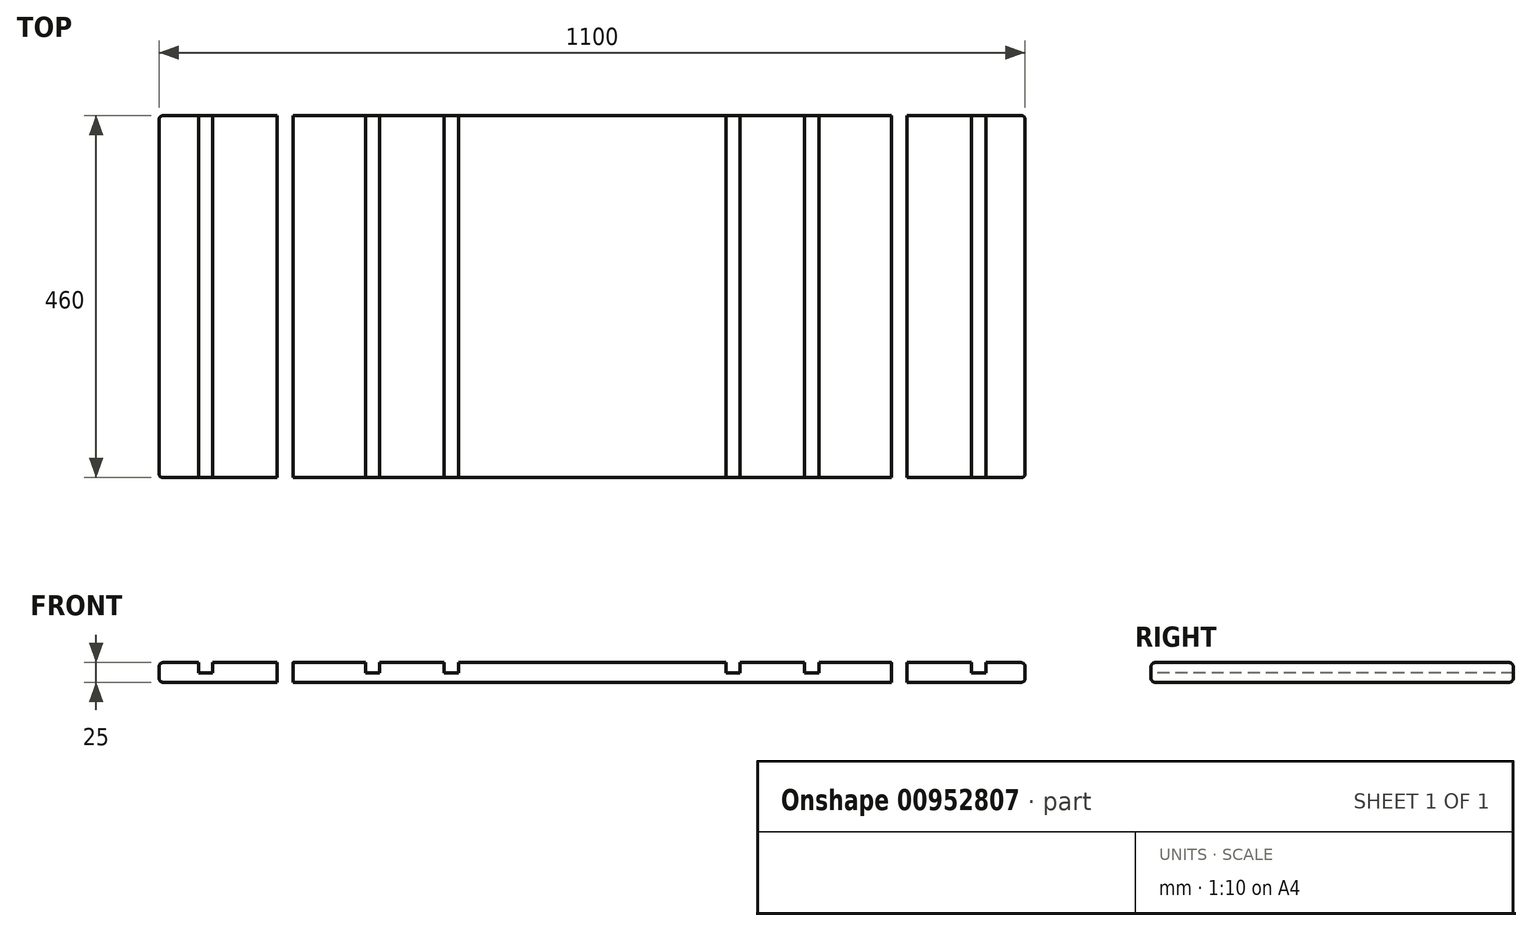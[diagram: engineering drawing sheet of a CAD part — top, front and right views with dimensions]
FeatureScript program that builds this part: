
annotation { "Feature Type Name" : "Feature", "Feature Type Description" : "" }
export const myFeature = defineFeature(function(context is Context, id is Id, definition is map)
    precondition{}
    {
        {
            var Q0;
            Q0=qCreatedBy(makeId("Top.planeOp"),FACE);
            var sketch = newSketch(context, id + "F0", { "sketchPlane" : qUnion([Q0])});
            skLineSegment(sketch, "E0.bottom", {"start": v(-380, 230) * mm, "end": v(380, 230) * mm});
            skLineSegment(sketch, "E0.top", {"start": v(-380, -230) * mm, "end": v(380, -230) * mm});
            skLineSegment(sketch, "E0.left", {"start": v(-380, 230) * mm, "end": v(-380, -230) * mm});
            skLineSegment(sketch, "E0.right", {"start": v(380, 230) * mm, "end": v(380, -230) * mm});
            skPoint(sketch, "E0.middle", {"position": v(0, 0) * mm});
            skSolve(sketch);
        }
        {
            var Q0;
            Q0=makeQuery(id+"F0.imprint","IMPRINT",FACE,{"disambiguationData":[TD([[makeQuery(id+"F0.imprint","IMPRINT",EDGE,{"derivedFrom":sQuery(id+"F0.wireOp",EDGE,"E0.bottom")}),-1.0]])]});
            extrude(context, id + "F1", {"entities" : qUnion([Q0]), "depth" : 25 * mm, "offsetDistance" : 25 * mm});
        }
        {
            var Q0;
            Q0=makeQuery(id+"F1.opExtrude","CAP_EDGE",EDGE,{"disambiguationData":[OSD([sQuery(id+"F0.wireOp",EDGE,"E0.top")])],"isStart":false});
            var Q1;
            Q1=makeQuery(id+"F1.opExtrude","CAP_EDGE",EDGE,{"disambiguationData":[OSD([sQuery(id+"F0.wireOp",EDGE,"E0.bottom")])],"isStart":false});
            var Q2;
            Q2=makeQuery(id+"F1.opExtrude","CAP_EDGE",EDGE,{"disambiguationData":[OSD([sQuery(id+"F0.wireOp",EDGE,"E0.bottom")])],"isStart":true});
            var Q3;
            Q3=makeQuery(id+"F1.opExtrude","CAP_EDGE",EDGE,{"disambiguationData":[OSD([sQuery(id+"F0.wireOp",EDGE,"E0.top")])],"isStart":true});
            fillet(context, id + "F2", {"entities" : qUnion([Q0, Q1, Q2, Q3]), "radius" : 5 * mm, "tangentPropagation" : true, "allowEdgeOverflow" : false});
        }
        {
            var Q0;
            Q0=qCreatedBy(makeId("Front.planeOp"),FACE);
            var sketch = newSketch(context, id + "F3", { "sketchPlane" : qUnion([Q0])});
            skLineSegment(sketch, "E1", {"start": v(0, 0) * mm, "end": v(-170, 0) * mm, "construction": true});
            skLineSegment(sketch, "E2", {"start": v(-170, 0) * mm, "end": v(-270, 0) * mm, "construction": true});
            skLineSegment(sketch, "E3", {"start": v(-170, 0) * mm, "end": v(-170, 25) * mm, "construction": true});
            skLineSegment(sketch, "E4", {"start": v(-270, 0) * mm, "end": v(-270, 25) * mm, "construction": true});
            skLineSegment(sketch, "E5", {"start": v(0, 0) * mm, "end": v(0, 16.31) * mm, "construction": true});
            skLineSegment(sketch, "E6.bottom", {"start": v(-170, 25) * mm, "end": v(-188, 25) * mm});
            skLineSegment(sketch, "E6.top", {"start": v(-170, 12) * mm, "end": v(-188, 12) * mm});
            skLineSegment(sketch, "E6.left", {"start": v(-170, 25) * mm, "end": v(-170, 12) * mm});
            skLineSegment(sketch, "E6.right", {"start": v(-188, 25) * mm, "end": v(-188, 12) * mm});
            skLineSegment(sketch, "E7.bottom", {"start": v(-270, 25) * mm, "end": v(-288, 25) * mm});
            skLineSegment(sketch, "E7.top", {"start": v(-270, 12) * mm, "end": v(-288, 12) * mm});
            skLineSegment(sketch, "E7.left", {"start": v(-270, 25) * mm, "end": v(-270, 12) * mm});
            skLineSegment(sketch, "E7.right", {"start": v(-288, 25) * mm, "end": v(-288, 12) * mm});
            skLineSegment(sketch, "E8.MirrorCS", {"start": v(170, 25) * mm, "end": v(170, 12) * mm});
            skLineSegment(sketch, "E9.MirrorCS", {"start": v(270, 25) * mm, "end": v(270, 12) * mm});
            skLineSegment(sketch, "E10.MirrorCS", {"start": v(170, 0) * mm, "end": v(170, 25) * mm, "construction": true});
            skLineSegment(sketch, "E11.MirrorCS", {"start": v(170, 0) * mm, "end": v(270, 0) * mm, "construction": true});
            skLineSegment(sketch, "E12.MirrorCS", {"start": v(170, 25) * mm, "end": v(188, 25) * mm});
            skLineSegment(sketch, "E13.MirrorCS", {"start": v(170, 12) * mm, "end": v(188, 12) * mm});
            skLineSegment(sketch, "E14.MirrorCS", {"start": v(270, 12) * mm, "end": v(288, 12) * mm});
            skLineSegment(sketch, "E15.MirrorCS", {"start": v(288, 25) * mm, "end": v(288, 12) * mm});
            skLineSegment(sketch, "E16.MirrorCS", {"start": v(188, 25) * mm, "end": v(188, 12) * mm});
            skLineSegment(sketch, "E17.MirrorCS", {"start": v(270, 25) * mm, "end": v(288, 25) * mm});
            skLineSegment(sketch, "E18.MirrorCS", {"start": v(270, 0) * mm, "end": v(270, 25) * mm, "construction": true});
            skSolve(sketch);
        }
        {
            var Q0;
            Q0 = qSketchRegion(id + "F3", true);
            extrude(context, id + "F4", {"entities" : qUnion([Q0]), "operationType" : NewBodyOperationType.REMOVE, "endBound" : BoundingType.SYMMETRIC, "oppositeDirection" : true, "depth" : 500 * mm, "offsetDistance" : 25 * mm});
        }
        {
            var Q0;
            Q0=qCreatedBy(makeId("Top.planeOp"),FACE);
            var sketch = newSketch(context, id + "F5", { "sketchPlane" : qUnion([Q0])});
            skLineSegment(sketch, "E19", {"start": v(0, 0) * mm, "end": v(-400, 0) * mm, "construction": true});
            skLineSegment(sketch, "E20", {"start": v(-400, 0) * mm, "end": v(-400, 230) * mm});
            skLineSegment(sketch, "E21", {"start": v(-400, 230) * mm, "end": v(-550, 230) * mm});
            skLineSegment(sketch, "E22", {"start": v(-550, 230) * mm, "end": v(-550, -230) * mm});
            skLineSegment(sketch, "E23", {"start": v(-550, -230) * mm, "end": v(-400, -230) * mm});
            skLineSegment(sketch, "E24", {"start": v(-400, -230) * mm, "end": v(-400, 0) * mm});
            skLineSegment(sketch, "E25", {"start": v(0, 0) * mm, "end": v(0, 33.9) * mm, "construction": true});
            skLineSegment(sketch, "E26.MirrorCS", {"start": v(400, -230) * mm, "end": v(400, 0) * mm});
            skLineSegment(sketch, "E27.MirrorCS", {"start": v(550, 230) * mm, "end": v(550, -230) * mm});
            skLineSegment(sketch, "E28.MirrorCS", {"start": v(400, 0) * mm, "end": v(400, 230) * mm});
            skLineSegment(sketch, "E29.MirrorCS", {"start": v(400, 230) * mm, "end": v(550, 230) * mm});
            skLineSegment(sketch, "E30.MirrorCS", {"start": v(550, -230) * mm, "end": v(400, -230) * mm});
            skSolve(sketch);
        }
        {
            var Q0;
            Q0=makeQuery(id+"F5.imprint","IMPRINT",FACE,{"disambiguationData":[TD([[makeQuery(id+"F5.imprint","IMPRINT",EDGE,{"derivedFrom":sQuery(id+"F5.wireOp",EDGE,"E20")}),1.0]])]});
            var Q1;
            Q1=makeQuery(id+"F5.imprint","IMPRINT",FACE,{"disambiguationData":[TD([[makeQuery(id+"F5.imprint","IMPRINT",EDGE,{"derivedFrom":sQuery(id+"F5.wireOp",EDGE,"E26.MirrorCS")}),-1.0]])]});
            extrude(context, id + "F6", {"entities" : qUnion([Q0, Q1]), "depth" : 25 * mm, "offsetDistance" : 25 * mm});
        }
        {
            var Q0;
            Q0=makeQuery(id+"F6.opExtrude","CAP_EDGE",EDGE,{"disambiguationData":[OSD([sQuery(id+"F5.wireOp",EDGE,"E21")])],"isStart":false});
            var Q1;
            Q1=makeQuery(id+"F6.opExtrude","CAP_EDGE",EDGE,{"disambiguationData":[OSD([sQuery(id+"F5.wireOp",EDGE,"E22")])],"isStart":false});
            var Q2;
            Q2=makeQuery(id+"F6.opExtrude","CAP_EDGE",EDGE,{"disambiguationData":[OSD([sQuery(id+"F5.wireOp",EDGE,"E23")])],"isStart":false});
            var Q3;
            Q3=makeQuery(id+"F6.opExtrude","CAP_EDGE",EDGE,{"disambiguationData":[OSD([sQuery(id+"F5.wireOp",EDGE,"E23")])],"isStart":true});
            var Q4;
            Q4=makeQuery(id+"F6.opExtrude","CAP_EDGE",EDGE,{"disambiguationData":[OSD([sQuery(id+"F5.wireOp",EDGE,"E22")])],"isStart":true});
            var Q5;
            Q5=makeQuery(id+"F6.opExtrude","CAP_EDGE",EDGE,{"disambiguationData":[OSD([sQuery(id+"F5.wireOp",EDGE,"E21")])],"isStart":true});
            var Q6;
            Q6=makeQuery(id+"F6.opExtrude","CAP_EDGE",EDGE,{"disambiguationData":[OSD([sQuery(id+"F5.wireOp",EDGE,"E29.MirrorCS")])],"isStart":true});
            var Q7;
            Q7=makeQuery(id+"F6.opExtrude","CAP_EDGE",EDGE,{"disambiguationData":[OSD([sQuery(id+"F5.wireOp",EDGE,"E27.MirrorCS")])],"isStart":true});
            var Q8;
            Q8=makeQuery(id+"F6.opExtrude","CAP_EDGE",EDGE,{"disambiguationData":[OSD([sQuery(id+"F5.wireOp",EDGE,"E30.MirrorCS")])],"isStart":true});
            var Q9;
            Q9=makeQuery(id+"F6.opExtrude","CAP_EDGE",EDGE,{"disambiguationData":[OSD([sQuery(id+"F5.wireOp",EDGE,"E29.MirrorCS")])],"isStart":false});
            var Q10;
            Q10=makeQuery(id+"F6.opExtrude","CAP_EDGE",EDGE,{"disambiguationData":[OSD([sQuery(id+"F5.wireOp",EDGE,"E30.MirrorCS")])],"isStart":false});
            var Q11;
            Q11=makeQuery(id+"F6.opExtrude","CAP_EDGE",EDGE,{"disambiguationData":[OSD([sQuery(id+"F5.wireOp",EDGE,"E27.MirrorCS")])],"isStart":false});
            var Q12;
            Q12=makeQuery(id+"F6.opExtrude","SWEPT_EDGE",EDGE,{"disambiguationData":[OSD([sQuery(id+"F5.wireOp",EDGE,"E27.MirrorCS"),sQuery(id+"F5.wireOp",EDGE,"E30.MirrorCS")])]});
            var Q13;
            Q13=makeQuery(id+"F6.opExtrude","SWEPT_EDGE",EDGE,{"disambiguationData":[OSD([sQuery(id+"F5.wireOp",EDGE,"E27.MirrorCS"),sQuery(id+"F5.wireOp",EDGE,"E29.MirrorCS")])]});
            var Q14;
            Q14=makeQuery(id+"F6.opExtrude","SWEPT_EDGE",EDGE,{"disambiguationData":[OSD([sQuery(id+"F5.wireOp",EDGE,"E22"),sQuery(id+"F5.wireOp",EDGE,"E23")])]});
            var Q15;
            Q15=makeQuery(id+"F6.opExtrude","SWEPT_EDGE",EDGE,{"disambiguationData":[OSD([sQuery(id+"F5.wireOp",EDGE,"E21"),sQuery(id+"F5.wireOp",EDGE,"E22")])]});
            fillet(context, id + "F7", {"entities" : qUnion([Q0, Q1, Q2, Q3, Q4, Q5, Q6, Q7, Q8, Q9, Q10, Q11, Q12, Q13, Q14, Q15]), "radius" : 5 * mm, "tangentPropagation" : true, "allowEdgeOverflow" : false});
        }
        {
            var Q0;
            Q0=qCreatedBy(makeId("Front.planeOp"),FACE);
            var sketch = newSketch(context, id + "F8", { "sketchPlane" : qUnion([Q0])});
            skLineSegment(sketch, "E31.0.0", {"start": v(-550, 0) * mm, "end": v(-425, 0) * mm, "construction": true});
            skLineSegment(sketch, "E31.0.1", {"start": v(-425, 0) * mm, "end": v(-400, 25) * mm, "construction": true});
            skLineSegment(sketch, "E31.0.2", {"start": v(-400, 25) * mm, "end": v(-550, 25) * mm, "construction": true});
            skLineSegment(sketch, "E31.0.3", {"start": v(-550, 25) * mm, "end": v(-550, 0) * mm, "construction": true});
            skLineSegment(sketch, "E32", {"start": v(-550, 25) * mm, "end": v(-500, 25) * mm, "construction": true});
            skLineSegment(sketch, "E33.bottom", {"start": v(-500, 25) * mm, "end": v(-482, 25) * mm});
            skLineSegment(sketch, "E33.top", {"start": v(-500, 12) * mm, "end": v(-482, 12) * mm});
            skLineSegment(sketch, "E33.left", {"start": v(-500, 25) * mm, "end": v(-500, 12) * mm});
            skLineSegment(sketch, "E33.right", {"start": v(-482, 25) * mm, "end": v(-482, 12) * mm});
            skLineSegment(sketch, "E34", {"start": v(0, 0) * mm, "end": v(0, 12.76) * mm, "construction": true});
            skLineSegment(sketch, "E35.MirrorCS", {"start": v(482, 25) * mm, "end": v(482, 12) * mm});
            skLineSegment(sketch, "E36.MirrorCS", {"start": v(500, 25) * mm, "end": v(500, 12) * mm});
            skLineSegment(sketch, "E37.MirrorCS", {"start": v(500, 25) * mm, "end": v(482, 25) * mm});
            skLineSegment(sketch, "E38.MirrorCS", {"start": v(550, 25) * mm, "end": v(500, 25) * mm, "construction": true});
            skLineSegment(sketch, "E39.MirrorCS", {"start": v(425, 0) * mm, "end": v(400, 25) * mm, "construction": true});
            skLineSegment(sketch, "E40.MirrorCS", {"start": v(500, 12) * mm, "end": v(482, 12) * mm});
            skLineSegment(sketch, "E41.MirrorCS", {"start": v(550, 0) * mm, "end": v(425, 0) * mm, "construction": true});
            skLineSegment(sketch, "E42.MirrorCS", {"start": v(550, 25) * mm, "end": v(550, 0) * mm, "construction": true});
            skLineSegment(sketch, "E43.MirrorCS", {"start": v(400, 25) * mm, "end": v(550, 25) * mm, "construction": true});
            skSolve(sketch);
        }
        {
            var Q0;
            Q0 = qSketchRegion(id + "F8", true);
            extrude(context, id + "F9", {"entities" : qUnion([Q0]), "operationType" : NewBodyOperationType.REMOVE, "endBound" : BoundingType.SYMMETRIC, "oppositeDirection" : true, "depth" : 500 * mm, "offsetDistance" : 25 * mm});
        }
    });
